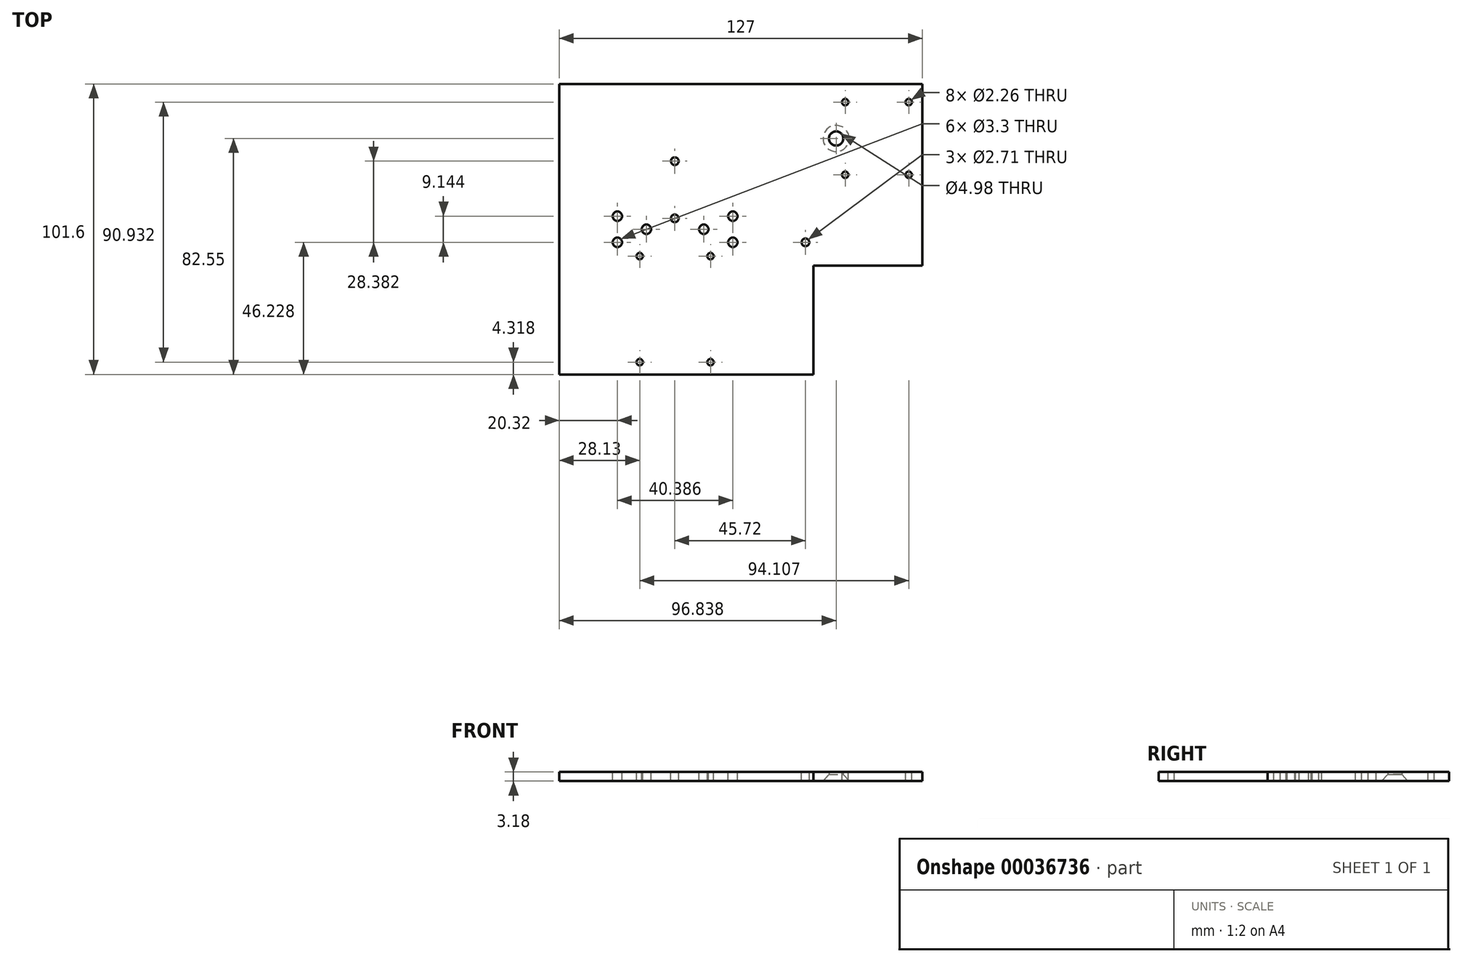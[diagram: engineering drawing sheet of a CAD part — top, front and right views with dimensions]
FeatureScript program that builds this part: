
annotation { "Feature Type Name" : "Feature", "Feature Type Description" : "" }
export const myFeature = defineFeature(function(context is Context, id is Id, definition is map)
    precondition{}
    {
        {
            var Q0;
            Q0=qCreatedBy(makeId("Front.planeOp"),FACE);
            var sketch = newSketch(context, id + "F0", { "sketchPlane" : qUnion([Q0])});
            skLineSegment(sketch, "E0", {"start": v(0, 0) * mm, "end": v(0, 3.18) * mm});
            skLineSegment(sketch, "E1", {"start": v(0, 3.18) * mm, "end": v(-127, 3.17) * mm});
            skLineSegment(sketch, "E2", {"start": v(-127, 3.17) * mm, "end": v(-127, 0) * mm});
            skLineSegment(sketch, "E3", {"start": v(-127, 0) * mm, "end": v(0, 0) * mm});
            skSolve(sketch);
        }
        {
            var Q0;
            Q0=makeQuery(id+"F0.imprint","IMPRINT",FACE,{"disambiguationData":[TD([[makeQuery(id+"F0.imprint","IMPRINT",EDGE,{"derivedFrom":sQuery(id+"F0.wireOp",EDGE,"E0")}),1.0]])]});
            extrude(context, id + "F1", {"entities" : qUnion([Q0]), "endBound" : BoundingType.SYMMETRIC, "depth" : 101.6 * mm, "offsetDistance" : 25.4 * mm});
        }
        {
            var Q0;
            Q0=makeQuery(id+"F1.opExtrude","SWEPT_FACE",FACE,{"disambiguationData":[OSD([sQuery(id+"F0.wireOp",EDGE,"E1")])]});
            var sketch = newSketch(context, id + "F2", { "sketchPlane" : qUnion([Q0])});
            skPoint(sketch, "E4", {"position": v(-106.68, 4.57) * mm});
            skPoint(sketch, "E5", {"position": v(-106.68, -4.57) * mm});
            skPoint(sketch, "E6", {"position": v(-96.52, 0) * mm});
            skPoint(sketch, "E7", {"position": v(-76.45, 0) * mm});
            skPoint(sketch, "E8", {"position": v(-66.3, 4.57) * mm});
            skPoint(sketch, "E9", {"position": v(-66.3, -4.57) * mm});
            skLineSegment(sketch, "E10", {"start": v(-127, 0) * mm, "end": v(-45.97, 0) * mm, "construction": true});
            skLineSegment(sketch, "E11", {"start": v(-86.49, 0) * mm, "end": v(-86.49, 9.55) * mm, "construction": true});
            skSolve(sketch);
        }
        {
            var Q0;
            Q0=sQuery(id+"F2.wireOp",VERTEX,"E8");
            var Q1;
            Q1=sQuery(id+"F2.wireOp",VERTEX,"E9");
            var Q2;
            Q2=sQuery(id+"F2.wireOp",VERTEX,"E7");
            var Q3;
            Q3=sQuery(id+"F2.wireOp",VERTEX,"E6");
            var Q4;
            Q4=sQuery(id+"F2.wireOp",VERTEX,"E4");
            var Q5;
            Q5=sQuery(id+"F2.wireOp",VERTEX,"E5");
            var Q6;
            Q6=makeQuery(id+"F1.opExtrude","SWEPT_BODY",BODY,{"disambiguationData":[OSD([sQuery(id+"F0.wireOp",EDGE,"E0"),sQuery(id+"F0.wireOp",EDGE,"f2e0e0e0-cd28-4836-966f-49551ec3c4cd"),sQuery(id+"F0.wireOp",EDGE,"6f173ce0-8d91-4cf6-bb4e-4d458c8b243f"),sQuery(id+"F0.wireOp",EDGE,"E1"),sQuery(id+"F0.wireOp",EDGE,"E2"),sQuery(id+"F0.wireOp",EDGE,"E3")])]});
            hole(context, id + "F3", {"style" : HoleStyle.SIMPLE, "endStyle" : HoleEndStyle.THROUGH, "holeDiameter" : 3.3 * mm, "majorDiameter" : 6.35 * mm, "tappedDepth" : 6.35 * mm, "tapClearance" : 3, "locations" : qUnion([Q0, Q1, Q2, Q3, Q4, Q5]), "scope" : qUnion([Q6])});
        }
        {
            var Q0;
            {var subQ0=sQuery(id+"F0.wireOp",EDGE,"E0");var subQ3=sQuery(id+"F0.wireOp",EDGE,"E1");Q0=makeQuery(id+"FpsT3sD0KDlX3Zd_3.boolean.opBoolean","SPLIT",FACE,{"disambiguationData":[TD([makeQuery(id+"F1.opExtrude","SWEPT_FACE",FACE,{"disambiguationData":[OSD([subQ0])]})])],"derivedFrom":makeQuery(id+"F1.opExtrude","SWEPT_FACE",FACE,{"disambiguationData":[OSD([subQ3])]})});}
            var sketch = newSketch(context, id + "F4", { "sketchPlane" : qUnion([Q0])});
            skLineSegment(sketch, "E12.bottom", {"start": v(0, -50.8) * mm, "end": v(-38.1, -50.8) * mm});
            skLineSegment(sketch, "E12.top", {"start": v(0, -12.7) * mm, "end": v(-38.1, -12.7) * mm});
            skLineSegment(sketch, "E12.left", {"start": v(0, -50.8) * mm, "end": v(0, -12.7) * mm});
            skLineSegment(sketch, "E12.right", {"start": v(-38.1, -50.8) * mm, "end": v(-38.1, -12.7) * mm});
            skSolve(sketch);
        }
        {
            var Q0;
            Q0=makeQuery(id+"F4.imprint","IMPRINT",FACE,{"disambiguationData":[TD([[makeQuery(id+"F4.imprint","IMPRINT",EDGE,{"derivedFrom":sQuery(id+"F4.wireOp",EDGE,"E12.bottom")}),-1.0]])]});
            extrude(context, id + "F5", {"entities" : qUnion([Q0]), "operationType" : NewBodyOperationType.REMOVE, "endBound" : BoundingType.THROUGH_ALL, "oppositeDirection" : true, "depth" : 25.4 * mm, "offsetDistance" : 25.4 * mm});
        }
        {
            var Q0;
            Q0=makeQuery(id+"F1.opExtrude","SWEPT_FACE",FACE,{"disambiguationData":[OSD([sQuery(id+"F0.wireOp",EDGE,"E1")])]});
            var sketch = newSketch(context, id + "F6", { "sketchPlane" : qUnion([Q0])});
            skPoint(sketch, "E13", {"position": v(-4.76, 44.45) * mm});
            skPoint(sketch, "E14", {"position": v(-26.99, 44.45) * mm});
            skPoint(sketch, "E15", {"position": v(-4.76, 19.05) * mm});
            skPoint(sketch, "E16", {"position": v(-26.99, 19.05) * mm});
            skSolve(sketch);
        }
        {
            var Q0;
            Q0=sQuery(id+"F6.wireOp",VERTEX,"E15");
            var Q1;
            Q1=sQuery(id+"F6.wireOp",VERTEX,"E16");
            var Q2;
            Q2=sQuery(id+"F6.wireOp",VERTEX,"E14");
            var Q3;
            Q3=sQuery(id+"F6.wireOp",VERTEX,"E13");
            var Q4;
            Q4=makeQuery(id+"F1.opExtrude","SWEPT_BODY",BODY,{"disambiguationData":[OSD([sQuery(id+"F0.wireOp",EDGE,"E0"),sQuery(id+"F0.wireOp",EDGE,"E1"),sQuery(id+"F0.wireOp",EDGE,"E2"),sQuery(id+"F0.wireOp",EDGE,"E3")])]});
            hole(context, id + "F7", {"style" : HoleStyle.SIMPLE, "endStyle" : HoleEndStyle.THROUGH, "standardTappedOrClearance" : lookupTablePath({ "standard" : "ANSI", "engagement" : "75%", "pitch" : "40 tpi", "size" : "#4", "type" : "Tapped" }), "standardBlindInLast" : lookupTablePath({ "standard" : "ANSI", "engagement" : "75%", "pitch" : "40 tpi", "size" : "#4", "type" : "Tapped" }), "holeDiameter" : 2.26 * mm, "majorDiameter" : 2.84 * mm, "showTappedDepth" : true, "isTappedThrough" : true, "tappedDepth" : 6.35 * mm, "tapClearance" : 3, "locations" : qUnion([Q0, Q1, Q2, Q3]), "scope" : qUnion([Q4])});
        }
        {
            var Q0;
            Q0=makeQuery(id+"F1.opExtrude","SWEPT_FACE",FACE,{"disambiguationData":[OSD([sQuery(id+"F0.wireOp",EDGE,"E1")])]});
            var sketch = newSketch(context, id + "F8", { "sketchPlane" : qUnion([Q0])});
            skSolve(sketch);
        }
        {
            var Q0;
            {var subQ0=sQuery(id+"F0.wireOp",EDGE,"E1");Q0=makeQuery(id+"F8.imprint","IMPRINT",FACE,{"disambiguationData":[TD([[makeQuery(id+"F8.imprint","IMPRINT",EDGE,{"derivedFrom":makeQuery(id+"F1.opExtrude","CAP_EDGE",EDGE,{"disambiguationData":[OSD([subQ0])],"isStart":true})}),1.0]])]});}
            var sketch = newSketch(context, id + "F9", { "sketchPlane" : qUnion([Q0])});
            skPoint(sketch, "E17", {"position": v(-98.87, -46.48) * mm});
            skPoint(sketch, "E18", {"position": v(-74.1, -46.48) * mm});
            skPoint(sketch, "E19", {"position": v(-74.1, -9.4) * mm});
            skPoint(sketch, "E20", {"position": v(-98.87, -9.4) * mm});
            skLineSegment(sketch, "E21", {"start": v(-74.1, -46.48) * mm, "end": v(-98.87, -46.48) * mm, "construction": true});
            skLineSegment(sketch, "E22", {"start": v(-86.49, -46.48) * mm, "end": v(-86.49, 20.15) * mm, "construction": true});
            skSolve(sketch);
        }
        {
            var Q0;
            Q0=sQuery(id+"F9.wireOp",VERTEX,"E18");
            var Q1;
            Q1=sQuery(id+"F9.wireOp",VERTEX,"E17");
            var Q2;
            Q2=sQuery(id+"F9.wireOp",VERTEX,"E20");
            var Q3;
            Q3=sQuery(id+"F9.wireOp",VERTEX,"E19");
            var Q4;
            Q4=makeQuery(id+"F1.opExtrude","SWEPT_BODY",BODY,{"disambiguationData":[OSD([sQuery(id+"F0.wireOp",EDGE,"E0"),sQuery(id+"F0.wireOp",EDGE,"E1"),sQuery(id+"F0.wireOp",EDGE,"E2"),sQuery(id+"F0.wireOp",EDGE,"E3")])]});
            hole(context, id + "F10", {"style" : HoleStyle.SIMPLE, "endStyle" : HoleEndStyle.THROUGH, "standardTappedOrClearance" : lookupTablePath({ "standard" : "ANSI", "engagement" : "75%", "pitch" : "40 tpi", "size" : "#4", "type" : "Tapped" }), "standardBlindInLast" : lookupTablePath({ "standard" : "ANSI", "engagement" : "75%", "pitch" : "40 tpi", "size" : "#4", "type" : "Tapped" }), "holeDiameter" : 2.26 * mm, "majorDiameter" : 2.84 * mm, "showTappedDepth" : true, "isTappedThrough" : true, "tappedDepth" : 6.35 * mm, "tapClearance" : 3, "locations" : qUnion([Q0, Q1, Q2, Q3]), "scope" : qUnion([Q4])});
        }
        {
            var Q0;
            {var subQ0=sQuery(id+"F0.wireOp",EDGE,"E1");Q0=makeQuery(id+"F8.imprint","IMPRINT",FACE,{"disambiguationData":[TD([[makeQuery(id+"F8.imprint","IMPRINT",EDGE,{"derivedFrom":makeQuery(id+"F1.opExtrude","CAP_EDGE",EDGE,{"disambiguationData":[OSD([subQ0])],"isStart":true})}),1.0]])]});}
            var sketch = newSketch(context, id + "F11", { "sketchPlane" : qUnion([Q0])});
            skPoint(sketch, "E23", {"position": v(-86.61, 3.8) * mm});
            skPoint(sketch, "E24", {"position": v(-86.61, 23.8) * mm});
            skPoint(sketch, "E25", {"position": v(-40.9, -4.57) * mm});
            skCircle(sketch, "E26.0", {"center": v(-66.3, -4.57) * mm, "radius": 1.65 * mm});
            skCircle(sketch, "E27.0", {"center": v(-76.45, 0) * mm, "radius": 1.65 * mm});
            skSolve(sketch);
        }
        {
            var Q0;
            Q0=sQuery(id+"F11.wireOp",VERTEX,"E25");
            var Q1;
            Q1=sQuery(id+"F11.wireOp",VERTEX,"E23");
            var Q2;
            Q2=sQuery(id+"F11.wireOp",VERTEX,"E24");
            var Q3;
            Q3=makeQuery(id+"F1.opExtrude","SWEPT_BODY",BODY,{"disambiguationData":[OSD([sQuery(id+"F0.wireOp",EDGE,"E0"),sQuery(id+"F0.wireOp",EDGE,"E1"),sQuery(id+"F0.wireOp",EDGE,"E2"),sQuery(id+"F0.wireOp",EDGE,"E3")])]});
            hole(context, id + "F12", {"style" : HoleStyle.SIMPLE, "endStyle" : HoleEndStyle.THROUGH, "standardTappedOrClearance" : lookupTablePath({ "standard" : "ANSI", "engagement" : "75%", "pitch" : "32 tpi", "size" : "#6", "type" : "Tapped" }), "standardBlindInLast" : lookupTablePath({ "standard" : "ANSI", "engagement" : "75%", "pitch" : "32 tpi", "size" : "#6", "type" : "Tapped" }), "holeDiameter" : 2.7 * mm, "majorDiameter" : 3.5 * mm, "showTappedDepth" : true, "isTappedThrough" : true, "tappedDepth" : 6.35 * mm, "tapClearance" : 3, "locations" : qUnion([Q0, Q1, Q2]), "scope" : qUnion([Q3])});
        }
        {
            var Q0;
            Q0=makeQuery(id+"F1.opExtrude","SWEPT_FACE",FACE,{"disambiguationData":[OSD([sQuery(id+"F0.wireOp",EDGE,"E3")])]});
            var sketch = newSketch(context, id + "F13", { "sketchPlane" : qUnion([Q0])});
            skCircle(sketch, "E28.0", {"center": v(-26.99, -44.45) * mm, "radius": 1.13 * mm});
            skPoint(sketch, "E29", {"position": v(-30.16, -31.75) * mm});
            skSolve(sketch);
        }
        {
            var Q0;
            Q0=sQuery(id+"F13.wireOp",VERTEX,"E29");
            var Q1;
            Q1=makeQuery(id+"F1.opExtrude","SWEPT_BODY",BODY,{"disambiguationData":[OSD([sQuery(id+"F0.wireOp",EDGE,"E0"),sQuery(id+"F0.wireOp",EDGE,"E1"),sQuery(id+"F0.wireOp",EDGE,"E2"),sQuery(id+"F0.wireOp",EDGE,"E3")])]});
            hole(context, id + "F14", {"style" : HoleStyle.C_SINK, "endStyle" : HoleEndStyle.THROUGH, "standardTappedOrClearance" : lookupTablePath({ "fit" : "Normal (ASME)", "standard" : "ANSI", "size" : "#8", "type" : "Clearance" }), "standardBlindInLast" : lookupTablePath({ "fit" : "Normal", "standard" : "ANSI", "size" : "#8", "type" : "Clearance" }), "holeDiameter" : 4.98 * mm, "cSinkDiameter" : 9.12 * mm, "cSinkAngle" : 82 * degree, "majorDiameter" : 4.17 * mm, "isTappedThrough" : true, "tappedDepth" : 6.35 * mm, "tapClearance" : 3, "locations" : qUnion([Q0]), "scope" : qUnion([Q1])});
        }
    });
